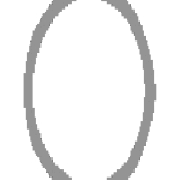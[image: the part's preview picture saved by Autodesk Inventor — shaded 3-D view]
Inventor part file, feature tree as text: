
AUTODESK INVENTOR PART (.ipt)
format: ipt  version: 2021 (Build 250183000, 183)  size: 109,568 bytes
history: native  units: in
note: dims shown in document units (in); Inventor stores cm internally (conversion verified against a paired STEP export)
features: other x4, sketch x3, plane x1
ambient origin geometry x8: Origin, YZ Plane, XZ Plane, XY Plane, X Axis, Y Axis, Z Axis, Center Point
bodies: Solid1 (feature_tree), Body (feature_tree)
feature tree (8):
  other  "Driven Length"
  other  "Frame Generator"
  other  "Start Plane"
  other  "End Plane"
  sketch  "Sketch"  dims[d2=28.9in d4=-0.0in d5=28.9in d6=0.12in d7=0.0in d8=90.0deg d9=28.9in]
  sketch  "Sketch2"  dims[d0=1.0in]
  plane  "Work Plane3"
  sketch  "Sketch3"  dims[d1=0.065in]
